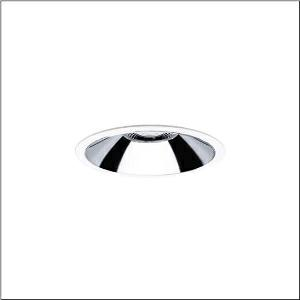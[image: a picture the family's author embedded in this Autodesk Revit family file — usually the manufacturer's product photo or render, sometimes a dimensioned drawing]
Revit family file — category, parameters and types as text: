
# Revit family: lunis_21_xl_51db15df42
name_source: partatom
category: Lighting Fixtures
units: mm (PartAtom-declared; Revit-internal decimal feet)

## family parameters
Cut with Voids When Loaded = No
Host = Face
Light Source = No
Part Type = Normal
Room Calculation Point = No
Round Connector Dimension = Use Diameter
Shared = No

## types (1)
- Lunis 21 XL (1 x LED, 2280 lm, 17.7 W, 4000K)
    Apparent Load = 18 VA
    CIE Flux Codes = 89 99 100 100 100
    Color Rendering = 80
    Color Temperature = 4000K
    Default Elevation = 1800 mm
    Description = Lunis 21,  XL, downlight, of PC, light emission: direct distribution, LED rated luminous flux: 2.280lm, light colour: 840, control gear: ECG DALI, with terminal, 5-pole, mains connection: 220..240V, AC, housing, round, of diecast aluminium, traffic white (RAL 9016), diameter: 213mm, protection rating (complete): IP20, protection rating (on room side): IP54, insulation class (complete): insulation class II (safety insulation), certification: CE, impact resistance: IK02, packaging unit: 1 piece
    Height = 0 mm  [stored 0 ft]
    Lamp = 1 x LED
    Lamp Light Flux = 2280 lm
    Lamp Power = 17.7 W
    Lamp count = 1
    Length = 213 mm
    Luminous efficacy = 129 lm/W
    Manufacturer = Siteco
    ModVariant = No
    Model = 51DB15DF42
    Mounting Place = Ceiling
    Mounting Type = Recessed
    Number of Poles = 1
    OnlyDefault = Yes
    Power Factor = 1
    Product Name = Lunis 21 XL
    Product group = downlight
    ProductGroupID = 400
    Protection Class = Protection class II
    Protection Degree = IP 20
    RLX_Detail_Level = 1
    RLX_Emergency_Light_Flux = 0 lm
    RLX_Emergency_Type = 0
    RLX_Emergency_Type_DB = No
    RlxData = <blob elided: 26945 chars, md5=7b52ddb0>
    Socket = socket
    Standby Power = 0 W
    System Light Flux = 2280 lm
    System Power = 18 W
    Type Comments = Product without accessories
    Type Image = l_1287385.jpg
    URL = http://relux.com
    VarID = ---
    Voltage = 0 V
    Weight = 0.00 kg
    Width = 0 mm  [stored 0 ft]

note: [stored X ft] marks values corroborated as IEEE doubles in the binary element streams (Revit-internal decimal feet)

## geometry (parser evidence)
native form markers: Blend x4, Sweep x10
no freeform markers — native parametric forms only
